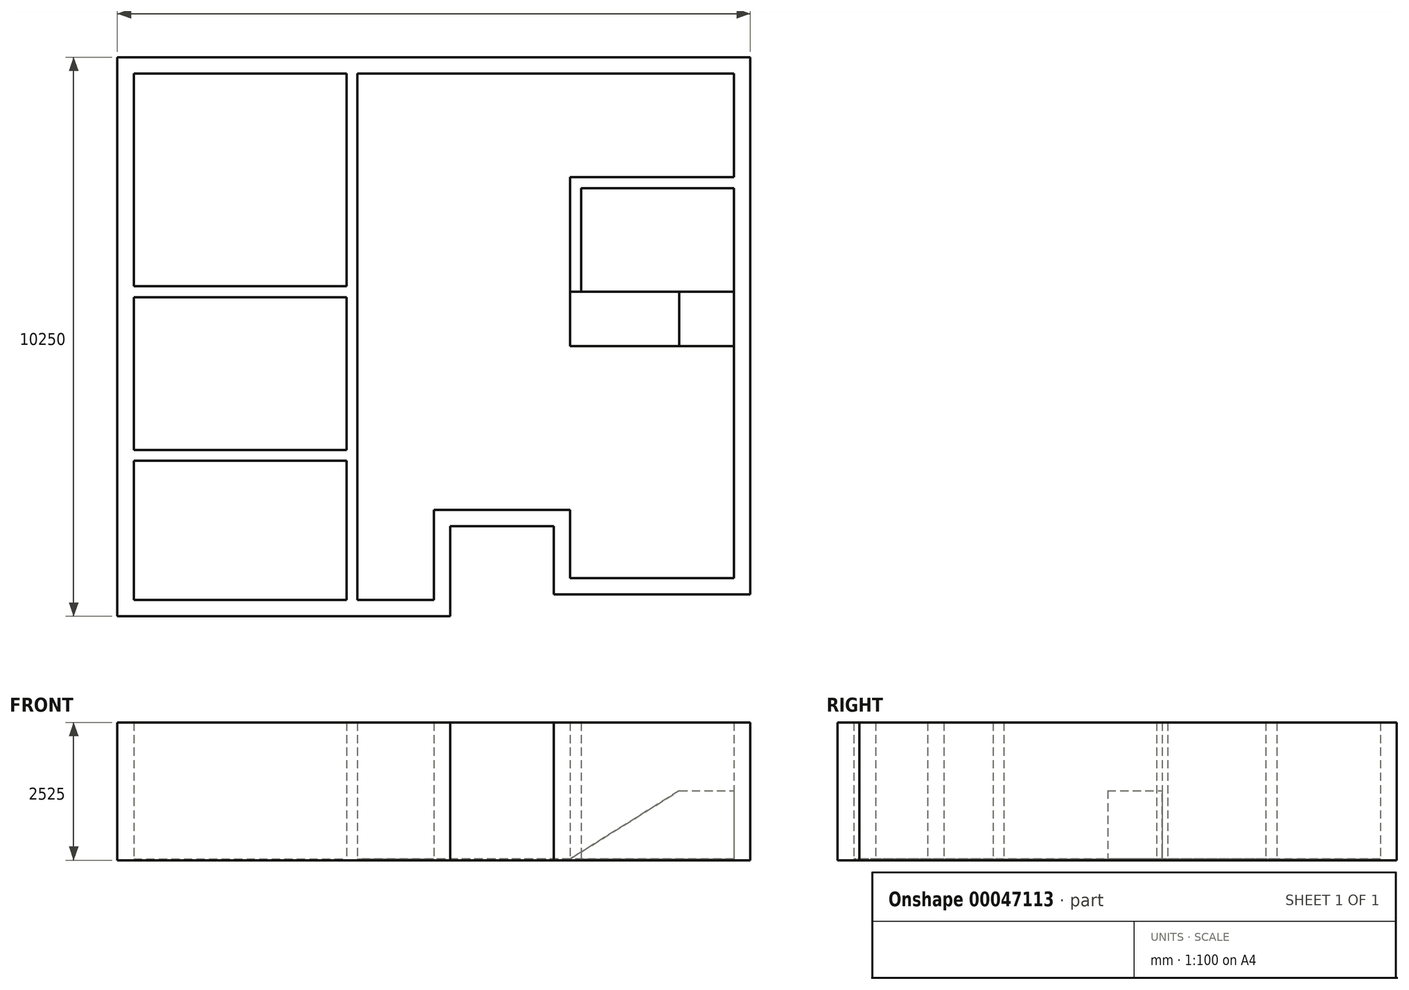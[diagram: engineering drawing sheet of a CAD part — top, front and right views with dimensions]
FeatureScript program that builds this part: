
annotation { "Feature Type Name" : "Feature", "Feature Type Description" : "" }
export const myFeature = defineFeature(function(context is Context, id is Id, definition is map)
    precondition{}
    {
        {
            var Q0;
            Q0=qCreatedBy(makeId("Top.planeOp"),FACE);
            var sketch = newSketch(context, id + "F0", { "sketchPlane" : qUnion([Q0])});
            skLineSegment(sketch, "E0.bottom", {"start": v(-3000, 0) * mm, "end": v(-5500, 0) * mm});
            skLineSegment(sketch, "E0.top", {"start": v(0, 8000) * mm, "end": v(-11000, 8000) * mm});
            skLineSegment(sketch, "E0.left", {"start": v(0, 0) * mm, "end": v(0, 8000) * mm});
            skLineSegment(sketch, "E0.right", {"start": v(-11000, 0) * mm, "end": v(-11000, 8000) * mm});
            skLineSegment(sketch, "E1.top", {"start": v(0, -1250) * mm, "end": v(-3000, -1250) * mm});
            skLineSegment(sketch, "E1.left", {"start": v(0, 0) * mm, "end": v(0, -1250) * mm});
            skLineSegment(sketch, "E1.right", {"start": v(-3000, 0) * mm, "end": v(-3000, -1250) * mm});
            skLineSegment(sketch, "E2.top", {"start": v(-11000, -1650) * mm, "end": v(-5500, -1650) * mm});
            skLineSegment(sketch, "E2.left", {"start": v(-11000, 0) * mm, "end": v(-11000, -1650) * mm});
            skLineSegment(sketch, "E2.right", {"start": v(-5500, 0) * mm, "end": v(-5500, -1650) * mm});
            skLineSegment(sketch, "E3.0", {"start": v(-11300, 2877.94) * mm, "end": v(-11300, -1950) * mm});
            skLineSegment(sketch, "E3.1", {"start": v(-11300, -1950) * mm, "end": v(-5200, -1950) * mm});
            skLineSegment(sketch, "E3.2", {"start": v(-11300, 2877.94) * mm, "end": v(-11300, 8300) * mm});
            skLineSegment(sketch, "E3.3", {"start": v(-5200, -300) * mm, "end": v(-5200, -1950) * mm});
            skLineSegment(sketch, "E3.4", {"start": v(-3300, -300) * mm, "end": v(-5200, -300) * mm});
            skLineSegment(sketch, "E3.5", {"start": v(-3300, -300) * mm, "end": v(-3300, -1550) * mm});
            skLineSegment(sketch, "E3.6", {"start": v(300, 8300) * mm, "end": v(-11300, 8300) * mm});
            skLineSegment(sketch, "E3.7", {"start": v(300, 2832.28) * mm, "end": v(300, 8300) * mm});
            skLineSegment(sketch, "E3.8", {"start": v(300, 2832.28) * mm, "end": v(300, -1550) * mm});
            skLineSegment(sketch, "E3.9", {"start": v(300, -1550) * mm, "end": v(-3300, -1550) * mm});
            skLineSegment(sketch, "E4", {"start": v(0, 6000) * mm, "end": v(-3000, 6000) * mm, "construction": true});
            skLineSegment(sketch, "E5", {"start": v(0, 3000) * mm, "end": v(-3000, 3000) * mm, "construction": true});
            skLineSegment(sketch, "E6.0", {"start": v(0, 6100) * mm, "end": v(-3000, 6100) * mm});
            skLineSegment(sketch, "E7.0", {"start": v(0, 5900) * mm, "end": v(-2800, 5900) * mm});
            skLineSegment(sketch, "E8", {"start": v(-3000, 6100) * mm, "end": v(-3000, 4000) * mm});
            skLineSegment(sketch, "E9", {"start": v(-3000, 4000) * mm, "end": v(-2800, 4000) * mm});
            skLineSegment(sketch, "E10", {"start": v(-2800, 4000) * mm, "end": v(-2800, 5900) * mm});
            skLineSegment(sketch, "E11", {"start": v(-3000, 4000) * mm, "end": v(-1000, 4000) * mm, "construction": true});
            skLineSegment(sketch, "E12", {"start": v(-1000, 4000) * mm, "end": v(-1000, 5900) * mm, "construction": true});
            skLineSegment(sketch, "E13", {"start": v(-7000, 8000) * mm, "end": v(-7000, -1650) * mm, "construction": true});
            skLineSegment(sketch, "E14", {"start": v(-7000, 1000) * mm, "end": v(-11000, 1000) * mm, "construction": true});
            skLineSegment(sketch, "E15", {"start": v(-7000, 4000) * mm, "end": v(-11000, 4000) * mm, "construction": true});
            skLineSegment(sketch, "E16.0", {"start": v(-6900, 8000) * mm, "end": v(-6900, -1650) * mm});
            skLineSegment(sketch, "E17.0", {"start": v(-7100, 8000) * mm, "end": v(-7100, -1650) * mm});
            skLineSegment(sketch, "E18.0", {"start": v(-7100, 4100) * mm, "end": v(-11000, 4100) * mm});
            skLineSegment(sketch, "E19.0", {"start": v(-7100, 3900) * mm, "end": v(-11000, 3900) * mm});
            skLineSegment(sketch, "E20.0", {"start": v(-7100, 1100) * mm, "end": v(-11000, 1100) * mm});
            skLineSegment(sketch, "E21.0", {"start": v(-7100, 900) * mm, "end": v(-11000, 900) * mm});
            skSolve(sketch);
        }
        {
            var Q0;
            Q0=makeQuery(id+"F0.imprint","IMPRINT",FACE,{"disambiguationData":[TD([[makeQuery(id+"F0.imprint","IMPRINT",EDGE,{"derivedFrom":sQuery(id+"F0.wireOp",EDGE,"E0.bottom")}),1.0]])]});
            var Q1;
            {var subQ9=sQuery(id+"F0.wireOp",EDGE,"E16.0");Q1=makeQuery(id+"F0.imprint","IMPRINT",FACE,{"disambiguationData":[TD([[makeQuery(id+"F0.imprint","IMPRINT",EDGE,{"derivedFrom":subQ9}),-1.0]])]});}
            var Q2;
            {var subQ2=sQuery(id+"F0.wireOp",EDGE,"E18.0");Q2=makeQuery(id+"F0.imprint","IMPRINT",FACE,{"disambiguationData":[TD([[makeQuery(id+"F0.imprint","IMPRINT",EDGE,{"derivedFrom":subQ2}),1.0]])]});}
            var Q3;
            {var subQ1=sQuery(id+"F0.wireOp",EDGE,"E20.0");Q3=makeQuery(id+"F0.imprint","IMPRINT",FACE,{"disambiguationData":[TD([[makeQuery(id+"F0.imprint","IMPRINT",EDGE,{"derivedFrom":subQ1}),1.0]])]});}
            var Q4;
            {var subQ2=sQuery(id+"F0.wireOp",EDGE,"E6.0");Q4=makeQuery(id+"F0.imprint","IMPRINT",FACE,{"disambiguationData":[TD([[makeQuery(id+"F0.imprint","IMPRINT",EDGE,{"derivedFrom":subQ2}),1.0]])]});}
            extrude(context, id + "F1", {"entities" : qUnion([Q0, Q1, Q2, Q3, Q4]), "depth" : 2500 * mm});
        }
        {
            var Q0;
            Q0=makeQuery(id+"F0.imprint","IMPRINT",FACE,{"disambiguationData":[TD([[makeQuery(id+"F0.imprint","IMPRINT",EDGE,{"derivedFrom":sQuery(id+"F0.wireOp",EDGE,"E0.bottom")}),1.0]])]});
            var Q1;
            {var subQ1=sQuery(id+"F0.wireOp",EDGE,"E20.0");Q1=makeQuery(id+"F0.imprint","IMPRINT",FACE,{"disambiguationData":[TD([[makeQuery(id+"F0.imprint","IMPRINT",EDGE,{"derivedFrom":subQ1}),1.0]])]});}
            var Q2;
            {var subQ2=sQuery(id+"F0.wireOp",EDGE,"E18.0");Q2=makeQuery(id+"F0.imprint","IMPRINT",FACE,{"disambiguationData":[TD([[makeQuery(id+"F0.imprint","IMPRINT",EDGE,{"derivedFrom":subQ2}),1.0]])]});}
            var Q3;
            {var subQ9=sQuery(id+"F0.wireOp",EDGE,"E16.0");Q3=makeQuery(id+"F0.imprint","IMPRINT",FACE,{"disambiguationData":[TD([[makeQuery(id+"F0.imprint","IMPRINT",EDGE,{"derivedFrom":subQ9}),-1.0]])]});}
            var Q4;
            {var subQ2=sQuery(id+"F0.wireOp",EDGE,"E6.0");Q4=makeQuery(id+"F0.imprint","IMPRINT",FACE,{"disambiguationData":[TD([[makeQuery(id+"F0.imprint","IMPRINT",EDGE,{"derivedFrom":subQ2}),1.0]])]});}
            var Q5;
            Q5=makeQuery(id+"F0.imprint","IMPRINT",FACE,{"disambiguationData":[TD([[makeQuery(id+"F0.imprint","IMPRINT",EDGE,{"derivedFrom":sQuery(id+"F0.wireOp",EDGE,"E0.bottom")}),-1.0]])]});
            var Q6;
            {var subQ1=sQuery(id+"F0.wireOp",EDGE,"E18.0");Q6=makeQuery(id+"F0.imprint","IMPRINT",FACE,{"disambiguationData":[TD([[makeQuery(id+"F0.imprint","IMPRINT",EDGE,{"derivedFrom":subQ1}),-1.0]])]});}
            var Q7;
            {var subQ1=sQuery(id+"F0.wireOp",EDGE,"E19.0");Q7=makeQuery(id+"F0.imprint","IMPRINT",FACE,{"disambiguationData":[TD([[makeQuery(id+"F0.imprint","IMPRINT",EDGE,{"derivedFrom":subQ1}),1.0]])]});}
            var Q8;
            {var subQ4=sQuery(id+"F0.wireOp",EDGE,"E2.left");Q8=makeQuery(id+"F0.imprint","IMPRINT",FACE,{"disambiguationData":[TD([[makeQuery(id+"F0.imprint","IMPRINT",EDGE,{"derivedFrom":subQ4}),1.0]])]});}
            extrude(context, id + "F2", {"entities" : qUnion([Q0, Q1, Q2, Q3, Q4, Q5, Q6, Q7, Q8]), "operationType" : NewBodyOperationType.ADD, "oppositeDirection" : true, "depth" : 25 * mm});
        }
        {
            var Q0;
            Q0=makeQuery(id+"F2.boolean.opBoolean","SPLIT",FACE,{"disambiguationData":[TD([makeQuery(id+"F1.opExtrude","SWEPT_FACE",FACE,{"disambiguationData":[OSD([sQuery(id+"F0.wireOp",EDGE,"E0.bottom")])]})])],"derivedFrom":makeQuery(id+"F2.opExtrude","CAP_FACE",FACE,{"disambiguationData":[OSD([sQuery(id+"F0.wireOp",EDGE,"E3.0"),sQuery(id+"F0.wireOp",EDGE,"E3.1"),sQuery(id+"F0.wireOp",EDGE,"E3.2"),sQuery(id+"F0.wireOp",EDGE,"E3.3"),sQuery(id+"F0.wireOp",EDGE,"E3.4"),sQuery(id+"F0.wireOp",EDGE,"E3.5"),sQuery(id+"F0.wireOp",EDGE,"E3.6"),sQuery(id+"F0.wireOp",EDGE,"E3.7"),sQuery(id+"F0.wireOp",EDGE,"E3.8"),sQuery(id+"F0.wireOp",EDGE,"E3.9")])],"isStart":true})});
            var sketch = newSketch(context, id + "F3", { "sketchPlane" : qUnion([Q0])});
            skLineSegment(sketch, "E22.0", {"start": v(0, 3000) * mm, "end": v(-3000, 3000) * mm});
            skLineSegment(sketch, "E23.0", {"start": v(-3000, 4000) * mm, "end": v(-1000, 4000) * mm});
            skLineSegment(sketch, "E24", {"start": v(-3000, 3000) * mm, "end": v(-3000, 4000) * mm});
            skLineSegment(sketch, "E25", {"start": v(-1000, 4000) * mm, "end": v(-1000, 3000) * mm});
            skLineSegment(sketch, "E26", {"start": v(-1000, 4000) * mm, "end": v(0, 4000) * mm});
            skLineSegment(sketch, "E27", {"start": v(0, 4000) * mm, "end": v(0, 3000) * mm});
            skSolve(sketch);
        }
        {
            var Q0;
            {var subQ1=sQuery(id+"F3.wireOp",EDGE,"E25");Q0=makeQuery(id+"F3.imprint","IMPRINT",FACE,{"disambiguationData":[TD([[makeQuery(id+"F3.imprint","IMPRINT",EDGE,{"derivedFrom":subQ1}),1.0]])]});}
            var Q1;
            {var subQ2=sQuery(id+"F3.wireOp",EDGE,"E24");Q1=makeQuery(id+"F3.imprint","IMPRINT",FACE,{"disambiguationData":[TD([[makeQuery(id+"F3.imprint","IMPRINT",EDGE,{"derivedFrom":subQ2}),-1.0]])]});}
            extrude(context, id + "F4", {"entities" : qUnion([Q0, Q1]), "operationType" : NewBodyOperationType.ADD, "depth" : 1250 * mm});
        }
        {
            var Q0;
            Q0=makeQuery(id+"F4.opExtrude","CAP_EDGE",EDGE,{"disambiguationData":[OSD([sQuery(id+"F3.wireOp",EDGE,"E24")])],"isStart":false});
            chamfer(context, id + "F5", {"entities" : qUnion([Q0]), "chamferType" : ChamferType.TWO_OFFSETS, "width1" : 1250 * mm, "oppositeDirection" : false, "width2" : 2000 * mm, "tangentPropagation" : true});
        }
    });
